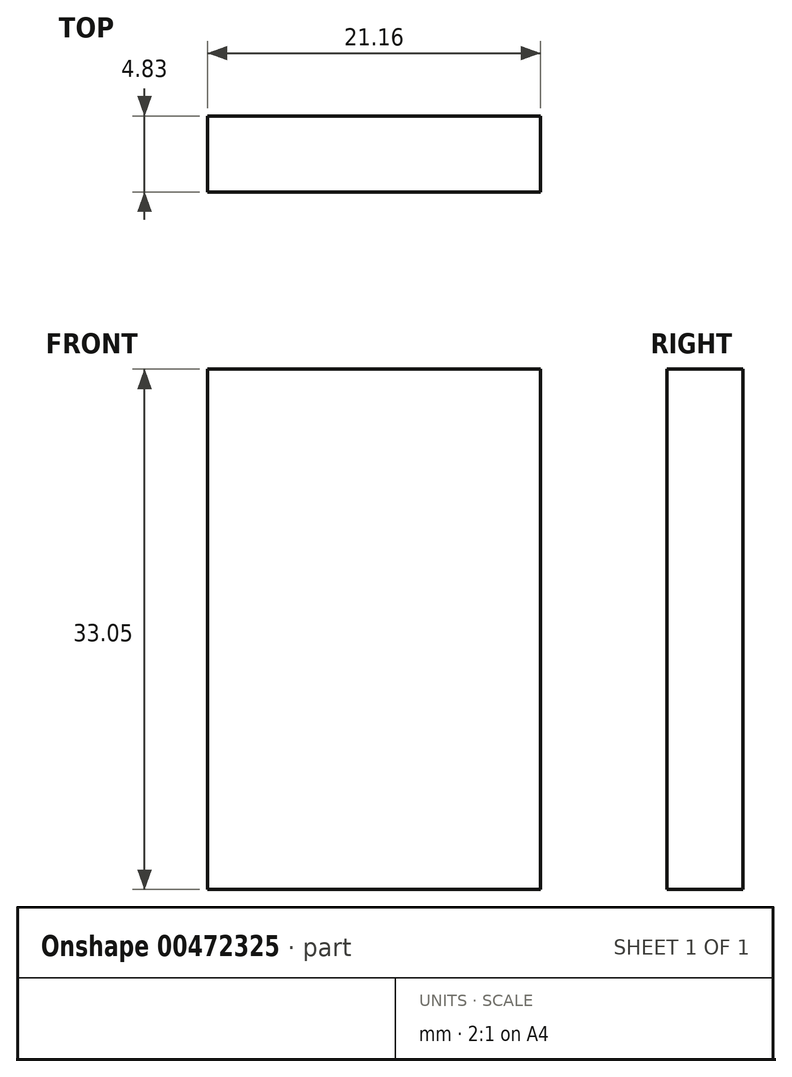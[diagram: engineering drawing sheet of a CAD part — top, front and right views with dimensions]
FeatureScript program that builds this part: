
annotation { "Feature Type Name" : "Feature", "Feature Type Description" : "" }
export const myFeature = defineFeature(function(context is Context, id is Id, definition is map)
    precondition{}
    {
        {
            var Q0;
            Q0=qCreatedBy(makeId("Front.planeOp"),FACE);
            var sketch = newSketch(context, id + "F0", { "sketchPlane" : qUnion([Q0])});
            skLineSegment(sketch, "E0.bottom", {"start": v(0, 0) * mm, "end": v(21.16, 0) * mm});
            skLineSegment(sketch, "E0.top", {"start": v(0, 33.05) * mm, "end": v(21.16, 33.05) * mm});
            skLineSegment(sketch, "E0.left", {"start": v(0, 0) * mm, "end": v(0, 33.05) * mm});
            skLineSegment(sketch, "E0.right", {"start": v(21.16, 0) * mm, "end": v(21.16, 33.05) * mm});
            skSolve(sketch);
        }
        {
            var Q0;
            Q0 = qSketchRegion(id + "F0", true);
            extrude(context, id + "F1", {"entities" : qUnion([Q0]), "depth" : 4.83 * mm, "offsetDistance" : 25.4 * mm});
        }
    });
